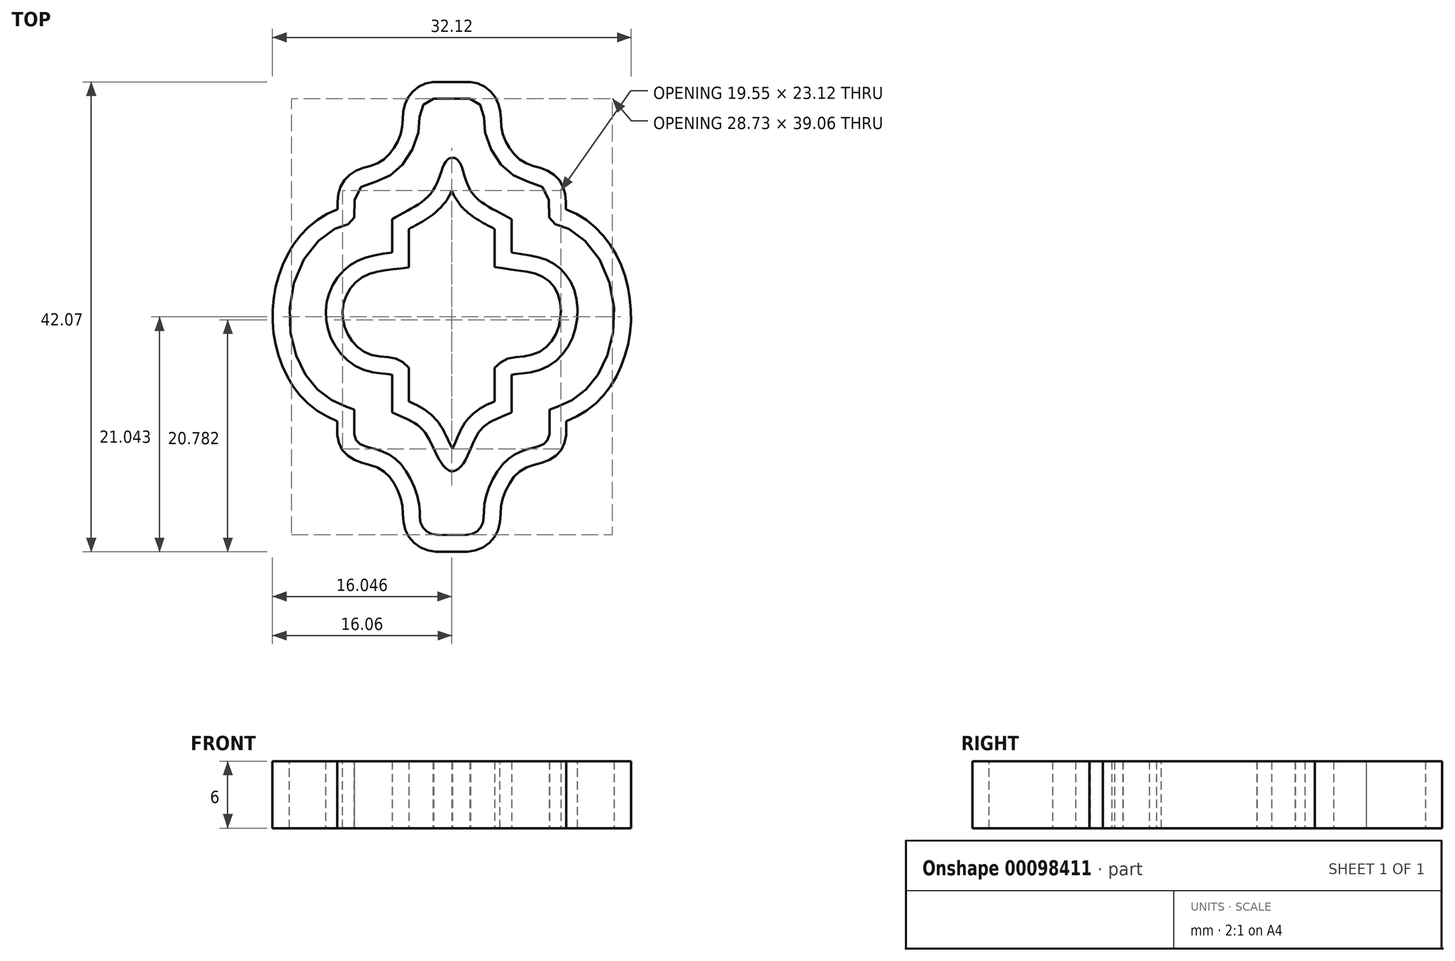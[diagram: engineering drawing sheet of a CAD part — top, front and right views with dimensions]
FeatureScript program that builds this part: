
annotation { "Feature Type Name" : "Feature", "Feature Type Description" : "" }
export const myFeature = defineFeature(function(context is Context, id is Id, definition is map)
    precondition{}
    {
        {
            var Q0;
            Q0=qCreatedBy(makeId("Top.planeOp"),FACE);
            var sketch = newSketch(context, id + "F0", { "sketchPlane" : qUnion([Q0]), "disableImprinting" : false});
            skLineSegment(sketch, "E0", {"start": v(0, -26.73) * mm, "end": v(1.63, -26.73) * mm});
            skFitSpline(sketch, "E1", {"points": [v(1.63, -26.73) * mm, v(2.73, -27.6) * mm, v(2.98, -29.71) * mm, v(4.4, -32.62) * mm, v(6.53, -34.07) * mm, v(8.53, -35.08) * mm, v(8.81, -37.7) * mm, v(9.75, -38.06) * mm, v(12.87, -40.54) * mm, v(14.55, -46.55) * mm, v(13.06, -51.5) * mm, v(10.63, -53.79) * mm, v(8.81, -54.53) * mm, v(8.75, -54.58) * mm], "startDerivative": vector(24.2, -1.57) * mm, "endDerivative": vector(9.21, -2.4) * mm});
            skLineSegment(sketch, "E2", {"start": v(8.75, -54.58) * mm, "end": v(8.75, -56.76) * mm});
            skFitSpline(sketch, "E3", {"points": [v(8.75, -56.76) * mm, v(7.93, -57.78) * mm, v(6.25, -58.3) * mm, v(4.3, -59.78) * mm, v(2.92, -63.04) * mm, v(2.77, -64.75) * mm, v(1.95, -65.65) * mm, v(0, -65.79) * mm], "startDerivative": vector(-1.8, -16.17) * mm, "endDerivative": vector(-18.96, 0.02) * mm});
            skLineSegment(sketch, "E4", {"start": v(0, -22.09) * mm, "end": v(0, -72.78) * mm, "construction": true});
            skLineSegment(sketch, "E5.MirrorCS", {"start": v(0, -26.73) * mm, "end": v(-1.63, -26.73) * mm});
            skFitSpline(sketch, "E6.MirrorCS", {"points": [v(-1.63, -26.73) * mm, v(-2.73, -27.6) * mm, v(-2.98, -29.71) * mm, v(-4.4, -32.62) * mm, v(-6.53, -34.07) * mm, v(-8.53, -35.08) * mm, v(-8.81, -37.7) * mm, v(-9.75, -38.06) * mm, v(-12.87, -40.54) * mm, v(-14.55, -46.55) * mm, v(-13.06, -51.5) * mm, v(-10.63, -53.79) * mm, v(-8.81, -54.53) * mm, v(-8.75, -54.58) * mm], "startDerivative": vector(-24.2, -1.57) * mm, "endDerivative": vector(-9.21, -2.4) * mm});
            skFitSpline(sketch, "E7.MirrorCS", {"points": [v(-8.75, -56.76) * mm, v(-7.93, -57.78) * mm, v(-6.25, -58.3) * mm, v(-4.3, -59.78) * mm, v(-2.92, -63.04) * mm, v(-2.77, -64.75) * mm, v(-1.95, -65.65) * mm, v(0, -65.79) * mm], "startDerivative": vector(1.8, -16.17) * mm, "endDerivative": vector(18.96, 0.02) * mm});
            skLineSegment(sketch, "E8", {"start": v(-8.75, -56.76) * mm, "end": v(-8.75, -54.58) * mm});
            skSolve(sketch);
        }
        {
            var Q0;
            Q0=makeQuery(id+"F0.imprint","IMPRINT",FACE,{"disambiguationData":[TD([[makeQuery(id+"F0.imprint","IMPRINT",EDGE,{"derivedFrom":sQuery(id+"F0.wireOp",EDGE,"E0")}),-1.0]])]});
            var Q1;
            Q1=sQuery(id+"F0.wireOp",EDGE,"E6.MirrorCS");
            var Q2;
            Q2=sQuery(id+"F0.wireOp",EDGE,"E1");
            var Q3;
            Q3=sQuery(id+"F0.wireOp",EDGE,"E0");
            var Q4;
            Q4=sQuery(id+"F0.wireOp",EDGE,"E5.MirrorCS");
            var Q5;
            Q5=sQuery(id+"F0.wireOp",EDGE,"E3");
            var Q6;
            Q6=sQuery(id+"F0.wireOp",EDGE,"E2");
            var Q7;
            Q7=sQuery(id+"F0.wireOp",EDGE,"E8");
            var Q8;
            Q8=sQuery(id+"F0.wireOp",EDGE,"E7.MirrorCS");
            extrude(context, id + "F1", {"entities" : qUnion([Q0]), "surfaceEntities" : qUnion([Q1, Q2, Q3, Q4, Q5, Q6, Q7, Q8]), "depth" : 6 * mm, "offsetDistance" : 25 * mm});
        }
        {
            var Q0;
            Q0=makeQuery(id+"F1.opExtrude","SWEPT_BODY",BODY,{"disambiguationData":[OSD([sQuery(id+"F0.wireOp",EDGE,"E0"),sQuery(id+"F0.wireOp",EDGE,"E1"),sQuery(id+"F0.wireOp",EDGE,"E2"),sQuery(id+"F0.wireOp",EDGE,"E3"),sQuery(id+"F0.wireOp",EDGE,"E5.MirrorCS"),sQuery(id+"F0.wireOp",EDGE,"E6.MirrorCS"),sQuery(id+"F0.wireOp",EDGE,"E7.MirrorCS"),sQuery(id+"F0.wireOp",EDGE,"E8")])]});
            transform(context, id + "F2", {"entities" : qUnion([Q0]), "transformType" : TransformType.TRANSLATION_3D, "dx" : 0 * mm, "dy" : 0 * mm, "dz" : 0 * mm, "makeCopy" : true});
        }
        {
            var Q0;
            Q0=makeQuery(id+"F1.opExtrude","CAP_FACE",FACE,{"disambiguationData":[OSD([sQuery(id+"F0.wireOp",EDGE,"E0"),sQuery(id+"F0.wireOp",EDGE,"E1"),sQuery(id+"F0.wireOp",EDGE,"E2"),sQuery(id+"F0.wireOp",EDGE,"E3"),sQuery(id+"F0.wireOp",EDGE,"E5.MirrorCS"),sQuery(id+"F0.wireOp",EDGE,"E6.MirrorCS"),sQuery(id+"F0.wireOp",EDGE,"E7.MirrorCS"),sQuery(id+"F0.wireOp",EDGE,"E8")])],"isStart":false});
            var Q1;
            Q1=makeQuery(id+"F1.opExtrude","CAP_FACE",FACE,{"disambiguationData":[OSD([sQuery(id+"F0.wireOp",EDGE,"E0"),sQuery(id+"F0.wireOp",EDGE,"E1"),sQuery(id+"F0.wireOp",EDGE,"E2"),sQuery(id+"F0.wireOp",EDGE,"E3"),sQuery(id+"F0.wireOp",EDGE,"E5.MirrorCS"),sQuery(id+"F0.wireOp",EDGE,"E6.MirrorCS"),sQuery(id+"F0.wireOp",EDGE,"E7.MirrorCS"),sQuery(id+"F0.wireOp",EDGE,"E8")])],"isStart":true});
            shell(context, id + "F3", {"entities" : qUnion([Q0, Q1]), "thickness" : 1.5 * mm, "oppositeDirection" : true});
        }
        {
            var Q0;
            Q0=qCreatedBy(makeId("Top.planeOp"),FACE);
            var sketch = newSketch(context, id + "F4", { "sketchPlane" : qUnion([Q0])});
            skFitSpline(sketch, "E9", {"points": [v(0, -32.01) * mm, v(1.57, -34.77) * mm, v(5.35, -37.52) * mm], "startDerivative": vector(6.45, 0.6) * mm, "endDerivative": vector(7.83, -4.72) * mm});
            skLineSegment(sketch, "E10", {"start": v(5.35, -37.52) * mm, "end": v(5.35, -40.5) * mm});
            skFitSpline(sketch, "E11", {"points": [v(5.35, -40.5) * mm, v(8.9, -41.35) * mm, v(11.02, -44.02) * mm, v(10.73, -48.33) * mm, v(7.74, -51.06) * mm, v(5.35, -51.47) * mm, v(5.35, -51.56) * mm], "startDerivative": vector(19.36, -2.75) * mm, "endDerivative": vector(1.56, -2.96) * mm});
            skLineSegment(sketch, "E12", {"start": v(5.35, -51.47) * mm, "end": v(5.35, -54.81) * mm});
            skFitSpline(sketch, "E13", {"points": [v(5.35, -54.81) * mm, v(2.42, -56.6) * mm, v(0, -60.14) * mm], "startDerivative": vector(-6.6, -3.1) * mm, "endDerivative": vector(-7.76, -1.37) * mm});
            skFitSpline(sketch, "E14.MirrorCS", {"points": [v(0, -32.01) * mm, v(-1.57, -34.77) * mm, v(-5.35, -37.52) * mm], "startDerivative": vector(-5.27, 0.07) * mm, "endDerivative": vector(-7.83, -4.72) * mm});
            skLineSegment(sketch, "E15.MirrorCS", {"start": v(-5.35, -37.52) * mm, "end": v(-5.35, -40.5) * mm});
            skFitSpline(sketch, "E16.MirrorCS", {"points": [v(-5.35, -40.5) * mm, v(-8.87, -41.47) * mm, v(-11.1, -44.53) * mm, v(-10.73, -48.33) * mm, v(-7.74, -51.06) * mm, v(-5.35, -51.47) * mm, v(-5.35, -51.56) * mm], "startDerivative": vector(-18.9, -2.16) * mm, "endDerivative": vector(-1.56, -2.96) * mm});
            skLineSegment(sketch, "E17.MirrorCS", {"start": v(-5.35, -51.47) * mm, "end": v(-5.35, -54.81) * mm});
            skFitSpline(sketch, "E18.MirrorCS", {"points": [v(-5.35, -54.81) * mm, v(-2.42, -56.6) * mm, v(0, -60.14) * mm], "startDerivative": vector(6.6, -3.1) * mm, "endDerivative": vector(6.75, -2.27) * mm});
            skSolve(sketch);
        }
        {
            var Q0;
            Q0 = qSketchRegion(id + "F4", true);
            extrude(context, id + "F5", {"entities" : qUnion([Q0]), "depth" : 6 * mm, "offsetDistance" : 25 * mm});
        }
        {
            var Q0;
            Q0=makeQuery(id+"F5.opExtrude","CAP_FACE",FACE,{"disambiguationData":[OSD([sQuery(id+"F4.wireOp",EDGE,"E9"),sQuery(id+"F4.wireOp",EDGE,"E10"),sQuery(id+"F4.wireOp",EDGE,"E11"),sQuery(id+"F4.wireOp",EDGE,"E12"),sQuery(id+"F4.wireOp",EDGE,"E13"),sQuery(id+"F4.wireOp",EDGE,"E14.MirrorCS"),sQuery(id+"F4.wireOp",EDGE,"E15.MirrorCS"),sQuery(id+"F4.wireOp",EDGE,"E16.MirrorCS"),sQuery(id+"F4.wireOp",EDGE,"E17.MirrorCS"),sQuery(id+"F4.wireOp",EDGE,"E18.MirrorCS")])],"isStart":false});
            var Q1;
            Q1=makeQuery(id+"F5.opExtrude","CAP_FACE",FACE,{"disambiguationData":[OSD([sQuery(id+"F4.wireOp",EDGE,"E9"),sQuery(id+"F4.wireOp",EDGE,"E10"),sQuery(id+"F4.wireOp",EDGE,"E11"),sQuery(id+"F4.wireOp",EDGE,"E12"),sQuery(id+"F4.wireOp",EDGE,"E13"),sQuery(id+"F4.wireOp",EDGE,"E14.MirrorCS"),sQuery(id+"F4.wireOp",EDGE,"E15.MirrorCS"),sQuery(id+"F4.wireOp",EDGE,"E16.MirrorCS"),sQuery(id+"F4.wireOp",EDGE,"E17.MirrorCS"),sQuery(id+"F4.wireOp",EDGE,"E18.MirrorCS")])],"isStart":true});
            shell(context, id + "F6", {"entities" : qUnion([Q0, Q1]), "thickness" : 1.5 * mm});
        }
        {
            var Q0;
            Q0=makeQuery(id+"F2.opPattern","COPY",BODY,{"derivedFrom":makeQuery(id+"F1.opExtrude","SWEPT_BODY",BODY,{"disambiguationData":[OSD([sQuery(id+"F0.wireOp",EDGE,"E0"),sQuery(id+"F0.wireOp",EDGE,"E1"),sQuery(id+"F0.wireOp",EDGE,"E2"),sQuery(id+"F0.wireOp",EDGE,"E3"),sQuery(id+"F0.wireOp",EDGE,"E5.MirrorCS"),sQuery(id+"F0.wireOp",EDGE,"E6.MirrorCS"),sQuery(id+"F0.wireOp",EDGE,"E7.MirrorCS"),sQuery(id+"F0.wireOp",EDGE,"E8")])]}),"instanceName":"1"});
            deleteBodies(context, id + "F7", {"entities" : qUnion([Q0])});
        }
    });
